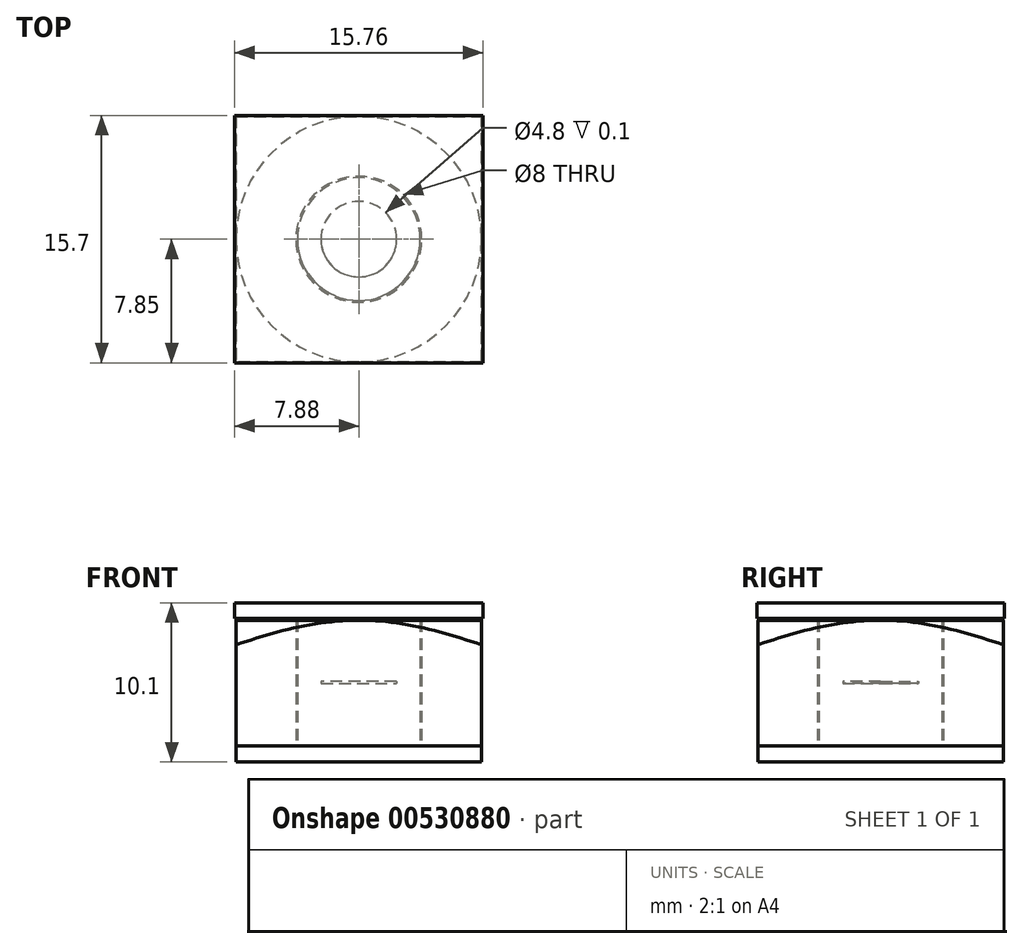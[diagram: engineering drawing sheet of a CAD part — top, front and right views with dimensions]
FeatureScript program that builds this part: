
annotation { "Feature Type Name" : "Feature", "Feature Type Description" : "" }
export const myFeature = defineFeature(function(context is Context, id is Id, definition is map)
    precondition{}
    {
        {
            var Q0;
            Q0=qCreatedBy(makeId("Top.planeOp"),FACE);
            var sketch = newSketch(context, id + "F0", { "sketchPlane" : qUnion([Q0])});
            skLineSegment(sketch, "E0.bottom", {"start": v(-7.8, -7.8) * mm, "end": v(7.8, -7.8) * mm});
            skLineSegment(sketch, "E0.top", {"start": v(-7.8, 7.8) * mm, "end": v(7.8, 7.8) * mm});
            skLineSegment(sketch, "E0.left", {"start": v(-7.8, -7.8) * mm, "end": v(-7.8, 7.8) * mm});
            skLineSegment(sketch, "E0.right", {"start": v(7.8, -7.8) * mm, "end": v(7.8, 7.8) * mm});
            skPoint(sketch, "E0.middle", {"position": v(0, 0) * mm});
            skCircle(sketch, "E1", {"center": v(0, 0) * mm, "radius": 4 * mm});
            skSolve(sketch);
        }
        {
            var Q0;
            Q0=makeQuery(id+"F0.imprint","IMPRINT",FACE,{"disambiguationData":[TD([[makeQuery(id+"F0.imprint","IMPRINT",EDGE,{"derivedFrom":sQuery(id+"F0.wireOp",EDGE,"E0.bottom")}),1.0]])]});
            extrude(context, id + "F1", {"entities" : qUnion([Q0]), "depth" : 8 * mm, "offsetDistance" : 25 * mm});
        }
        {
            var Q0;
            Q0=makeQuery(id+"F1.opExtrude","CAP_FACE",FACE,{"disambiguationData":[OSD([sQuery(id+"F0.wireOp",EDGE,"E0.bottom"),sQuery(id+"F0.wireOp",EDGE,"E0.top"),sQuery(id+"F0.wireOp",EDGE,"E0.left"),sQuery(id+"F0.wireOp",EDGE,"E0.right"),sQuery(id+"F0.wireOp",EDGE,"E1")])],"isStart":false});
            var sketch = newSketch(context, id + "F2", { "sketchPlane" : qUnion([Q0])});
            skCircle(sketch, "E2", {"center": v(0, 0) * mm, "radius": 7.8 * mm});
            skSolve(sketch);
        }
        {
            var Q0;
            Q0=qCreatedBy(makeId("Right.planeOp"),FACE);
            var sketch = newSketch(context, id + "F3", { "sketchPlane" : qUnion([Q0])});
            skLineSegment(sketch, "E3", {"start": v(-7.8, 8) * mm, "end": v(-11.3, 8) * mm});
            skLineSegment(sketch, "E4", {"start": v(-11.3, 8) * mm, "end": v(-11.3, 6.3) * mm});
            skLineSegment(sketch, "E5", {"start": v(-11.3, 6.3) * mm, "end": v(-7.8, 8) * mm});
            skSolve(sketch);
        }
        {
            var Q0;
            Q0=makeQuery(id+"F3.imprint","IMPRINT",FACE,{"disambiguationData":[TD([[makeQuery(id+"F3.imprint","IMPRINT",EDGE,{"derivedFrom":sQuery(id+"F3.wireOp",EDGE,"E3")}),1.0]])]});
            var Q1;
            Q1=sQuery(id+"F2.wireOp",EDGE,"E2");
            revolve(context, id + "F4", {"operationType" : NewBodyOperationType.REMOVE, "entities" : qUnion([Q0]), "axis" : qUnion([Q1]), "revolveType" : RevolveType.FULL, "oppositeDirection" : true});
        }
        {
            var Q0;
            Q0=makeQuery(id+"F1.opExtrude","CAP_FACE",FACE,{"disambiguationData":[OSD([sQuery(id+"F0.wireOp",EDGE,"E0.bottom"),sQuery(id+"F0.wireOp",EDGE,"E0.top"),sQuery(id+"F0.wireOp",EDGE,"E0.left"),sQuery(id+"F0.wireOp",EDGE,"E0.right"),sQuery(id+"F0.wireOp",EDGE,"E1")])],"isStart":true});
            var sketch = newSketch(context, id + "F5", { "sketchPlane" : qUnion([Q0])});
            skLineSegment(sketch, "E6.bottom", {"start": v(7.85, -7.85) * mm, "end": v(-7.85, -7.85) * mm});
            skLineSegment(sketch, "E6.top", {"start": v(7.85, 7.85) * mm, "end": v(-7.85, 7.85) * mm});
            skLineSegment(sketch, "E6.left", {"start": v(7.85, -7.85) * mm, "end": v(7.85, 7.85) * mm});
            skLineSegment(sketch, "E6.right", {"start": v(-7.85, -7.85) * mm, "end": v(-7.85, 7.85) * mm});
            skPoint(sketch, "E6.middle", {"position": v(0, 0) * mm});
            skCircle(sketch, "E7.0", {"center": v(0, 0) * mm, "radius": 3.9 * mm});
            skCircle(sketch, "E8.0", {"center": v(0, 0) * mm, "radius": 2.4 * mm});
            skSolve(sketch);
        }
        {
            var Q0;
            Q0=makeQuery(id+"F5.imprint","IMPRINT",FACE,{"disambiguationData":[TD([[makeQuery(id+"F5.imprint","IMPRINT",EDGE,{"derivedFrom":makeQuery(id+"F1.opExtrude","CAP_EDGE",EDGE,{"disambiguationData":[OSD([sQuery(id+"F0.wireOp",EDGE,"E0.bottom")])],"isStart":true})}),-1.0]])]});
            var Q1;
            Q1=makeQuery(id+"F5.imprint","IMPRINT",FACE,{"disambiguationData":[TD([[makeQuery(id+"F5.imprint","IMPRINT",EDGE,{"derivedFrom":sQuery(id+"F5.wireOp",EDGE,"E7.0")}),-1.0]])]});
            var Q2;
            Q2=makeQuery(id+"F5.imprint","IMPRINT",FACE,{"disambiguationData":[TD([[makeQuery(id+"F5.imprint","IMPRINT",EDGE,{"derivedFrom":sQuery(id+"F5.wireOp",EDGE,"E7.0")}),1.0]])]});
            var Q3;
            Q3=makeQuery(id+"F5.imprint","IMPRINT",FACE,{"disambiguationData":[TD([[makeQuery(id+"F5.imprint","IMPRINT",EDGE,{"derivedFrom":sQuery(id+"F5.wireOp",EDGE,"E8.0")}),1.0]])]});
            extrude(context, id + "F6", {"entities" : qUnion([Q0, Q1, Q2, Q3]), "depth" : 1 * mm, "offsetDistance" : 25 * mm});
        }
        {
            var Q0;
            Q0=makeQuery(id+"F5.imprint","IMPRINT",FACE,{"disambiguationData":[TD([[makeQuery(id+"F5.imprint","IMPRINT",EDGE,{"derivedFrom":sQuery(id+"F5.wireOp",EDGE,"E7.0")}),1.0]])]});
            extrude(context, id + "F7", {"entities" : qUnion([Q0]), "operationType" : NewBodyOperationType.ADD, "oppositeDirection" : true, "depth" : 8.1 * mm, "offsetDistance" : 25 * mm});
        }
        {
            var Q0;
            Q0=makeQuery(id+"F5.imprint","IMPRINT",FACE,{"disambiguationData":[TD([[makeQuery(id+"F5.imprint","IMPRINT",EDGE,{"derivedFrom":sQuery(id+"F5.wireOp",EDGE,"E8.0")}),1.0]])]});
            extrude(context, id + "F8", {"entities" : qUnion([Q0]), "operationType" : NewBodyOperationType.ADD, "oppositeDirection" : true, "depth" : 4 * mm, "offsetDistance" : 25 * mm});
        }
        {
            var Q0;
            Q0=makeQuery(id+"F7.opExtrude","CAP_FACE",FACE,{"disambiguationData":[OSD([sQuery(id+"F5.wireOp",EDGE,"E7.0"),sQuery(id+"F5.wireOp",EDGE,"E8.0")])],"isStart":false});
            var sketch = newSketch(context, id + "F9", { "sketchPlane" : qUnion([Q0])});
            skLineSegment(sketch, "E9.bottom", {"start": v(7.88, 7.85) * mm, "end": v(-7.88, 7.85) * mm});
            skLineSegment(sketch, "E9.top", {"start": v(7.88, -7.85) * mm, "end": v(-7.88, -7.85) * mm});
            skLineSegment(sketch, "E9.left", {"start": v(7.88, 7.85) * mm, "end": v(7.88, -7.85) * mm});
            skLineSegment(sketch, "E9.right", {"start": v(-7.88, 7.85) * mm, "end": v(-7.88, -7.85) * mm});
            skPoint(sketch, "E9.middle", {"position": v(0, 0) * mm});
            skSolve(sketch);
        }
        {
            var Q0;
            Q0=makeQuery(id+"F9.imprint","IMPRINT",FACE,{"disambiguationData":[TD([[makeQuery(id+"F9.imprint","IMPRINT",EDGE,{"derivedFrom":makeQuery(id+"F7.opExtrude","CAP_EDGE",EDGE,{"disambiguationData":[OSD([sQuery(id+"F5.wireOp",EDGE,"E8.0")])],"isStart":false})}),-1.0]])]});
            extrude(context, id + "F10", {"entities" : qUnion([Q0]), "oppositeDirection" : true, "depth" : 4 * mm, "offsetDistance" : 25 * mm});
        }
        {
            var Q0;
            Q0=makeQuery(id+"F9.imprint","IMPRINT",FACE,{"disambiguationData":[TD([[makeQuery(id+"F9.imprint","IMPRINT",EDGE,{"derivedFrom":sQuery(id+"F9.wireOp",EDGE,"E9.bottom")}),1.0]])]});
            var Q1;
            Q1=makeQuery(id+"F9.imprint","IMPRINT",FACE,{"disambiguationData":[TD([[makeQuery(id+"F9.imprint","IMPRINT",EDGE,{"derivedFrom":makeQuery(id+"F7.opExtrude","CAP_EDGE",EDGE,{"disambiguationData":[OSD([sQuery(id+"F5.wireOp",EDGE,"E7.0")])],"isStart":false})}),-1.0]])]});
            var Q2;
            Q2=makeQuery(id+"F9.imprint","IMPRINT",FACE,{"disambiguationData":[TD([[makeQuery(id+"F9.imprint","IMPRINT",EDGE,{"derivedFrom":makeQuery(id+"F7.opExtrude","CAP_EDGE",EDGE,{"disambiguationData":[OSD([sQuery(id+"F5.wireOp",EDGE,"E8.0")])],"isStart":false})}),-1.0]])]});
            extrude(context, id + "F11", {"entities" : qUnion([Q0, Q1, Q2]), "operationType" : NewBodyOperationType.ADD, "depth" : 1 * mm, "offsetDistance" : 25 * mm});
        }
    });
